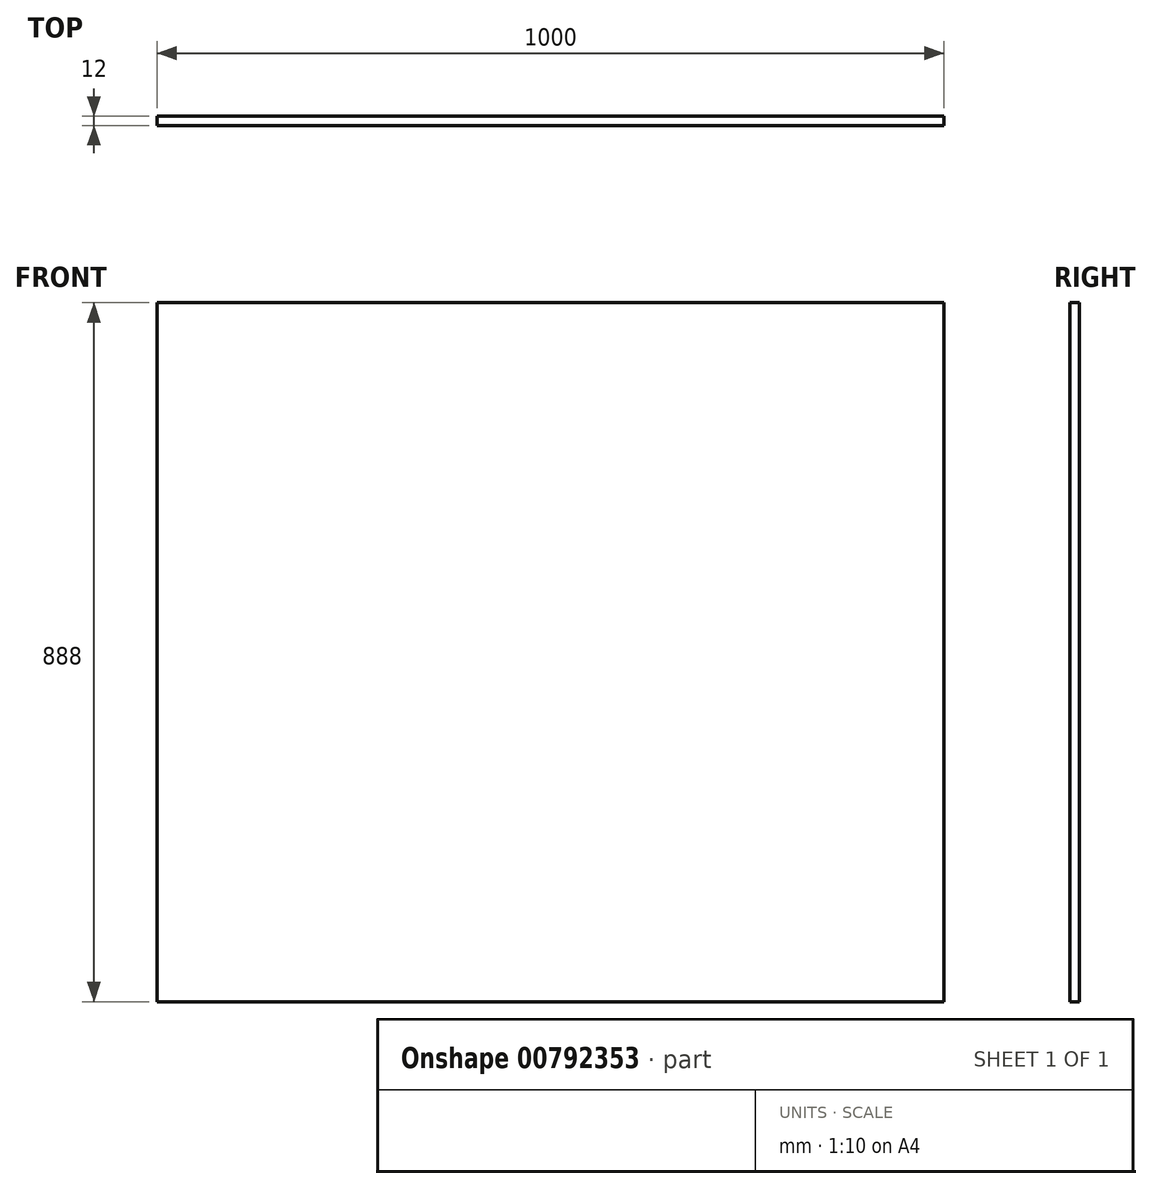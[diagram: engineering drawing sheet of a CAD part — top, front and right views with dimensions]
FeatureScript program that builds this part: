
annotation { "Feature Type Name" : "Feature", "Feature Type Description" : "" }
export const myFeature = defineFeature(function(context is Context, id is Id, definition is map)
    precondition{}
    {
        {
            var Q0;
            Q0=qCreatedBy(makeId("Front.planeOp"),FACE);
            var sketch = newSketch(context, id + "F0", { "sketchPlane" : qUnion([Q0])});
            skLineSegment(sketch, "E0.bottom", {"start": v(500, 444) * mm, "end": v(-500, 444) * mm});
            skLineSegment(sketch, "E0.top", {"start": v(500, -444) * mm, "end": v(-500, -444) * mm});
            skLineSegment(sketch, "E0.left", {"start": v(500, 444) * mm, "end": v(500, -444) * mm});
            skLineSegment(sketch, "E0.right", {"start": v(-500, 444) * mm, "end": v(-500, -444) * mm});
            skPoint(sketch, "E0.middle", {"position": v(0, 0) * mm});
            skSolve(sketch);
        }
        {
            var Q0;
            Q0 = qSketchRegion(id + "F0", true);
            extrude(context, id + "F1", {"entities" : qUnion([Q0]), "depth" : 12 * mm, "offsetDistance" : 25 * mm});
        }
    });
